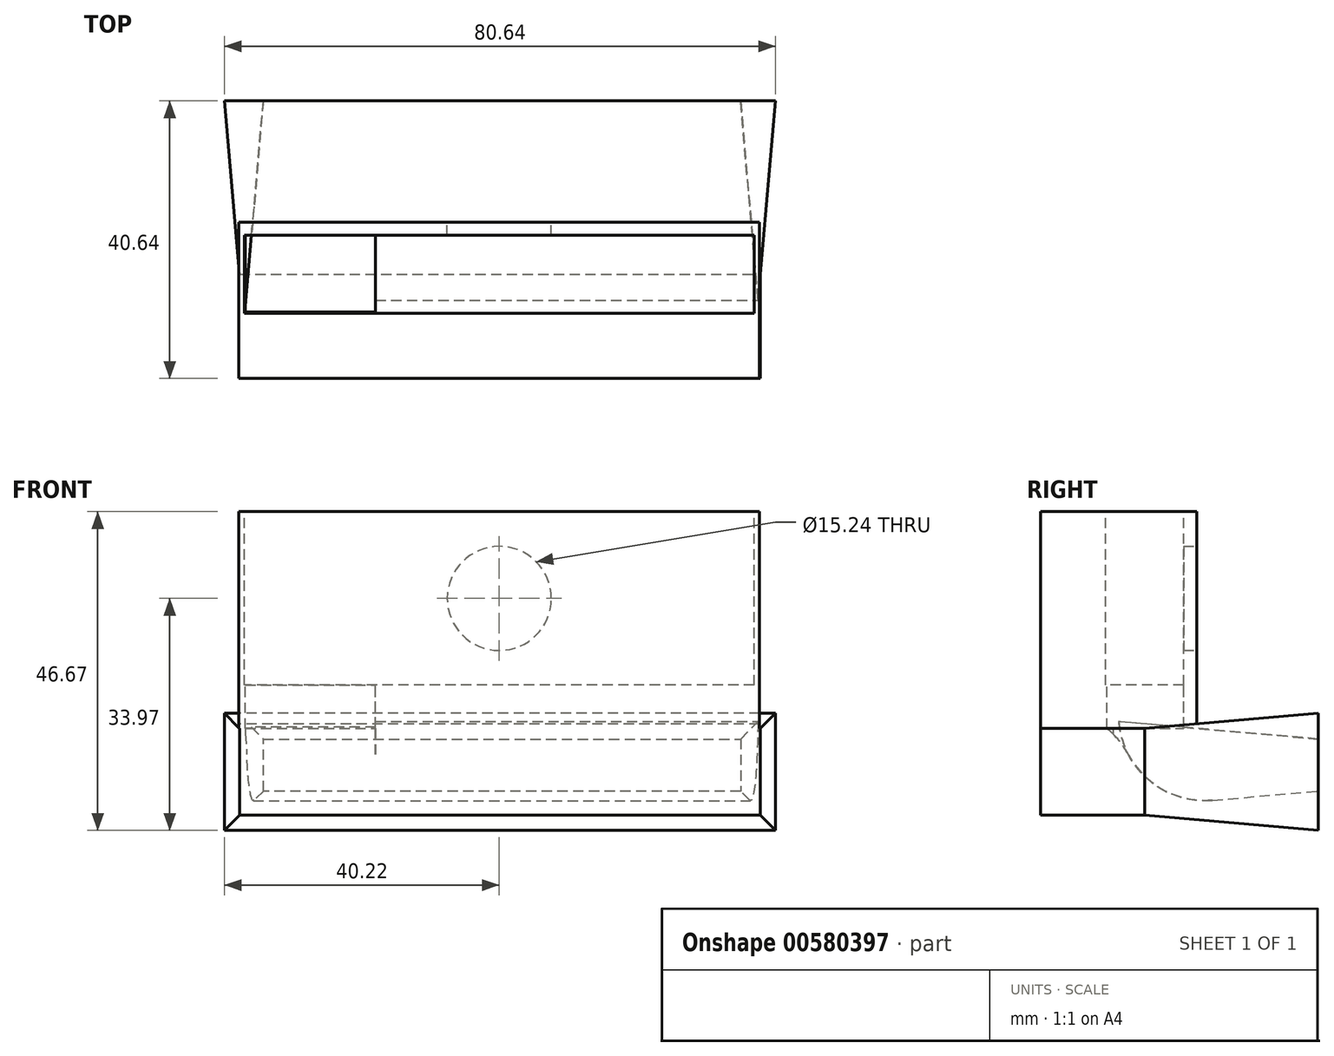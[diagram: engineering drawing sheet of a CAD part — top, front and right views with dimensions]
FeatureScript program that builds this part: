
annotation { "Feature Type Name" : "Feature", "Feature Type Description" : "" }
export const myFeature = defineFeature(function(context is Context, id is Id, definition is map)
    precondition{}
    {
        {
            var Q0;
            Q0=qCreatedBy(makeId("Top.planeOp"),FACE);
            var sketch = newSketch(context, id + "F0", { "sketchPlane" : qUnion([Q0])});
            skLineSegment(sketch, "E0.bottom", {"start": v(38.1, -7.62) * mm, "end": v(-38.1, -7.62) * mm});
            skLineSegment(sketch, "E0.top", {"start": v(38.1, 7.62) * mm, "end": v(-38.1, 7.62) * mm});
            skLineSegment(sketch, "E0.left", {"start": v(38.1, -7.62) * mm, "end": v(38.1, 7.62) * mm});
            skLineSegment(sketch, "E0.right", {"start": v(-38.1, -7.62) * mm, "end": v(-38.1, 7.62) * mm});
            skPoint(sketch, "E0.middle", {"position": v(0, 0) * mm});
            skSolve(sketch);
        }
        {
            var Q0;
            Q0 = qSketchRegion(id + "F0", true);
            extrude(context, id + "F1", {"entities" : qUnion([Q0]), "depth" : 31.75 * mm, "offsetDistance" : 25.4 * mm});
        }
        {
            var Q0;
            Q0=makeQuery(id+"F1.opExtrude","CAP_FACE",FACE,{"disambiguationData":[OSD([sQuery(id+"F0.wireOp",EDGE,"E0.bottom"),sQuery(id+"F0.wireOp",EDGE,"E0.top"),sQuery(id+"F0.wireOp",EDGE,"E0.left"),sQuery(id+"F0.wireOp",EDGE,"E0.right")])],"isStart":false});
            var sketch = newSketch(context, id + "F2", { "sketchPlane" : qUnion([Q0])});
            skLineSegment(sketch, "E1.bottom", {"start": v(37.31, 5.72) * mm, "end": v(-37.31, 5.72) * mm});
            skLineSegment(sketch, "E1.top", {"start": v(37.31, -5.72) * mm, "end": v(-37.31, -5.72) * mm});
            skLineSegment(sketch, "E1.left", {"start": v(37.31, 5.72) * mm, "end": v(37.31, -5.72) * mm});
            skLineSegment(sketch, "E1.right", {"start": v(-37.31, 5.72) * mm, "end": v(-37.31, -5.72) * mm});
            skPoint(sketch, "E1.middle", {"position": v(0, 0) * mm});
            skSolve(sketch);
        }
        {
            var Q0;
            Q0=makeQuery(id+"F2.imprint","IMPRINT",FACE,{"disambiguationData":[TD([[makeQuery(id+"F2.imprint","IMPRINT",EDGE,{"derivedFrom":sQuery(id+"F2.wireOp",EDGE,"E1.bottom")}),1.0]])]});
            extrude(context, id + "F3", {"entities" : qUnion([Q0]), "operationType" : NewBodyOperationType.REMOVE, "oppositeDirection" : true, "depth" : 25.4 * mm, "offsetDistance" : 25.4 * mm});
        }
        {
            var Q0;
            Q0=makeQuery(id+"F1.opExtrude","SWEPT_FACE",FACE,{"disambiguationData":[OSD([sQuery(id+"F0.wireOp",EDGE,"E0.top")])]});
            var sketch = newSketch(context, id + "F4", { "sketchPlane" : qUnion([Q0])});
            skLineSegment(sketch, "E2", {"start": v(0, 0) * mm, "end": v(0, 19.05) * mm});
            skPoint(sketch, "E2.endSnap0", {"position": v(0, 0) * mm});
            skLineSegment(sketch, "E3", {"start": v(0, 19.05) * mm, "end": v(-38.1, 19.05) * mm});
            skPoint(sketch, "E4", {"position": v(0, 19.05) * mm});
            skCircle(sketch, "E5", {"center": v(0, 19.05) * mm, "radius": 7.62 * mm});
            skSolve(sketch);
        }
        {
            var Q0;
            {var subQ0=sQuery(id+"F4.wireOp",EDGE,"E3");var subQ1=sQuery(id+"F4.wireOp",EDGE,"E2");var subQ2=makeQuery(id+"F4.imprint","INTERSECT",VERTEX,{"derivedFrom":[subQ1,subQ0]});Q0=makeQuery(id+"F4.imprint","IMPRINT",FACE,{"disambiguationData":[TD([[makeQuery(id+"F4.imprint","IMPRINT",EDGE,{"disambiguationData":[TD([[subQ2,1.0]])],"derivedFrom":subQ1}),-1.0]])]});}
            var Q1;
            {var subQ0=sQuery(id+"F4.wireOp",EDGE,"E3");var subQ1=sQuery(id+"F4.wireOp",EDGE,"E2");var subQ2=makeQuery(id+"F4.imprint","INTERSECT",VERTEX,{"derivedFrom":[subQ1,subQ0]});Q1=makeQuery(id+"F4.imprint","IMPRINT",FACE,{"disambiguationData":[TD([[makeQuery(id+"F4.imprint","IMPRINT",EDGE,{"disambiguationData":[TD([[subQ2,1.0]])],"derivedFrom":subQ1}),1.0]])]});}
            extrude(context, id + "F5", {"entities" : qUnion([Q0, Q1]), "operationType" : NewBodyOperationType.REMOVE, "oppositeDirection" : true, "depth" : 12.7 * mm, "offsetDistance" : 25.4 * mm});
        }
        {
            var Q0;
            Q0=makeQuery(id+"F3.boolean.opBoolean","COPY",FACE,{"derivedFrom":makeQuery(id+"F3.opExtrude","CAP_FACE",FACE,{"disambiguationData":[OSD([sQuery(id+"F2.wireOp",EDGE,"E1.bottom"),sQuery(id+"F2.wireOp",EDGE,"E1.top"),sQuery(id+"F2.wireOp",EDGE,"E1.left"),sQuery(id+"F2.wireOp",EDGE,"E1.right")])],"isStart":false})});
            var sketch = newSketch(context, id + "F6", { "sketchPlane" : qUnion([Q0])});
            skLineSegment(sketch, "E6.bottom", {"start": v(37.31, 5.72) * mm, "end": v(18.26, 5.72) * mm});
            skLineSegment(sketch, "E6.top", {"start": v(37.31, -5.72) * mm, "end": v(18.26, -5.72) * mm});
            skLineSegment(sketch, "E6.left", {"start": v(37.31, 5.72) * mm, "end": v(37.31, -5.72) * mm});
            skLineSegment(sketch, "E6.right", {"start": v(18.26, 5.71) * mm, "end": v(18.26, -5.72) * mm});
            skSolve(sketch);
        }
        {
            var Q0;
            Q0=qCreatedBy(makeId("Front.planeOp"),FACE);
            var sketch = newSketch(context, id + "F7", { "sketchPlane" : qUnion([Q0])});
            skLineSegment(sketch, "E7", {"start": v(-38, 0) * mm, "end": v(-38, -12.7) * mm});
            skLineSegment(sketch, "E8", {"start": v(-38, -12.7) * mm, "end": v(38.2, -12.7) * mm});
            skLineSegment(sketch, "E9", {"start": v(38.2, -12.7) * mm, "end": v(38.2, 0) * mm});
            skLineSegment(sketch, "E10", {"start": v(-38, 0) * mm, "end": v(38.2, 0) * mm});
            skSolve(sketch);
        }
        {
            var Q0;
            Q0=makeQuery(id+"F7.imprint","IMPRINT",FACE,{"disambiguationData":[TD([[makeQuery(id+"F7.imprint","IMPRINT",EDGE,{"derivedFrom":sQuery(id+"F7.wireOp",EDGE,"E7")}),1.0]])]});
            extrude(context, id + "F8", {"entities" : qUnion([Q0]), "operationType" : NewBodyOperationType.ADD, "depth" : 7.62 * mm, "offsetDistance" : 25.4 * mm});
        }
        {
            var Q0;
            Q0=makeQuery(id+"F8.opExtrude","CAP_FACE",FACE,{"disambiguationData":[OSD([sQuery(id+"F7.wireOp",EDGE,"E7"),sQuery(id+"F7.wireOp",EDGE,"E8"),sQuery(id+"F7.wireOp",EDGE,"E9"),sQuery(id+"F7.wireOp",EDGE,"E10")])],"isStart":true});
            extrude(context, id + "F9", {"entities" : qUnion([Q0]), "operationType" : NewBodyOperationType.ADD, "depth" : 25.4 * mm, "offsetDistance" : 25.4 * mm, "hasDraft" : true, "draftAngle" : 5 * degree});
        }
        {
            var Q0;
            Q0=makeQuery(id+"F9.opExtrude","CAP_FACE",FACE,{"disambiguationData":[OSD([sQuery(id+"F7.wireOp",EDGE,"E7"),sQuery(id+"F7.wireOp",EDGE,"E8"),sQuery(id+"F7.wireOp",EDGE,"E9"),sQuery(id+"F7.wireOp",EDGE,"E10")])],"isStart":false});
            var sketch = newSketch(context, id + "F10", { "sketchPlane" : qUnion([Q0])});
            skLineSegment(sketch, "E11.bottom", {"start": v(-35.3, -1.54) * mm, "end": v(34.54, -1.54) * mm});
            skLineSegment(sketch, "E11.top", {"start": v(-35.3, -9.16) * mm, "end": v(34.54, -9.16) * mm});
            skLineSegment(sketch, "E11.left", {"start": v(-35.3, -1.54) * mm, "end": v(-35.3, -9.16) * mm});
            skLineSegment(sketch, "E11.right", {"start": v(34.54, -1.54) * mm, "end": v(34.54, -9.16) * mm});
            skSolve(sketch);
        }
        {
            var Q0;
            Q0=makeQuery(id+"F10.imprint","IMPRINT",FACE,{"disambiguationData":[TD([[makeQuery(id+"F10.imprint","IMPRINT",EDGE,{"derivedFrom":sQuery(id+"F10.wireOp",EDGE,"E11.bottom")}),-1.0]])]});
            extrude(context, id + "F11", {"entities" : qUnion([Q0]), "operationType" : NewBodyOperationType.REMOVE, "oppositeDirection" : true, "depth" : 29.2 * mm, "offsetDistance" : 25.4 * mm, "hasDraft" : true, "draftAngle" : 5 * degree});
        }
        {
            var Q0;
            {var subQ0=sQuery(id+"F6.wireOp",EDGE,"E6.right");Q0=makeQuery(id+"F6.imprint","IMPRINT",FACE,{"disambiguationData":[TD([[makeQuery(id+"F6.imprint","IMPRINT",EDGE,{"derivedFrom":subQ0}),-1.0]])]});}
            var sketch = newSketch(context, id + "F12", { "sketchPlane" : qUnion([Q0])});
            skLineSegment(sketch, "E12.bottom", {"start": v(-37.17, 5.96) * mm, "end": v(-18.12, 5.96) * mm});
            skLineSegment(sketch, "E12.top", {"start": v(-37.17, -5.47) * mm, "end": v(-18.12, -5.47) * mm});
            skLineSegment(sketch, "E12.left", {"start": v(-37.17, 5.96) * mm, "end": v(-37.17, -5.47) * mm});
            skLineSegment(sketch, "E12.right", {"start": v(-18.12, 5.96) * mm, "end": v(-18.12, -5.47) * mm});
            skSolve(sketch);
        }
        {
            var Q0;
            {var subQ0=sQuery(id+"F12.wireOp",EDGE,"E12.top");Q0=makeQuery(id+"F12.imprint","IMPRINT",FACE,{"disambiguationData":[TD([[makeQuery(id+"F12.imprint","IMPRINT",EDGE,{"derivedFrom":subQ0}),1.0]])]});}
            extrude(context, id + "F13", {"entities" : qUnion([Q0]), "operationType" : NewBodyOperationType.REMOVE, "oppositeDirection" : true, "depth" : 6.35 * mm, "offsetDistance" : 25.4 * mm});
        }
        {
            var Q0;
            Q0=makeQuery(id+"F8.boolean.opBoolean","MERGE",FACE,{"derivedFrom":[makeQuery(id+"F1.opExtrude","SWEPT_FACE",FACE,{"disambiguationData":[OSD([sQuery(id+"F0.wireOp",EDGE,"E0.bottom")])]}),makeQuery(id+"F8.opExtrude","CAP_FACE",FACE,{"disambiguationData":[OSD([sQuery(id+"F7.wireOp",EDGE,"E7"),sQuery(id+"F7.wireOp",EDGE,"E8"),sQuery(id+"F7.wireOp",EDGE,"E9"),sQuery(id+"F7.wireOp",EDGE,"E10")])],"isStart":false})]});
            extrude(context, id + "F14", {"entities" : qUnion([Q0]), "operationType" : NewBodyOperationType.ADD, "depth" : 7.62 * mm, "offsetDistance" : 25.4 * mm});
        }
        {
            var Q0;
            Q0=makeQuery(id+"F11.boolean.opBoolean","COPY",EDGE,{"derivedFrom":makeQuery(id+"F11.opExtrude","CAP_EDGE",EDGE,{"disambiguationData":[OSD([sQuery(id+"F10.wireOp",EDGE,"E11.top")])],"isStart":false})});
            fillet(context, id + "F15", {"entities" : qUnion([Q0]), "radius" : 12.7 * mm, "tangentPropagation" : true, "allowEdgeOverflow" : false});
        }
        {
            var Q0;
            Q0=makeQuery(id+"F15.opFillet","BLEND_EDGE",EDGE,{"blendedFrom":[makeQuery(id+"F11.boolean.opBoolean","COPY",EDGE,{"derivedFrom":makeQuery(id+"F11.opExtrude","CAP_EDGE",EDGE,{"disambiguationData":[OSD([sQuery(id+"F10.wireOp",EDGE,"E11.top")])],"isStart":false})}),makeQuery(id+"F13.boolean.opBoolean","COPY",FACE,{"derivedFrom":makeQuery(id+"F13.opExtrude","CAP_FACE",FACE,{"disambiguationData":[OSD([sQuery(id+"F2.wireOp",EDGE,"E1.bottom"),sQuery(id+"F12.wireOp",EDGE,"E12.top"),sQuery(id+"F12.wireOp",EDGE,"E12.left"),sQuery(id+"F12.wireOp",EDGE,"E12.right")])],"isStart":false})})],"blendedInto":[makeQuery(id+"F13.boolean.opBoolean","COPY",FACE,{"derivedFrom":makeQuery(id+"F13.opExtrude","CAP_FACE",FACE,{"disambiguationData":[OSD([sQuery(id+"F2.wireOp",EDGE,"E1.bottom"),sQuery(id+"F12.wireOp",EDGE,"E12.top"),sQuery(id+"F12.wireOp",EDGE,"E12.left"),sQuery(id+"F12.wireOp",EDGE,"E12.right")])],"isStart":false})})]});
            fillet(context, id + "F16", {"entities" : qUnion([Q0]), "radius" : 12.7 * mm, "tangentPropagation" : true, "allowEdgeOverflow" : false});
        }
    });
